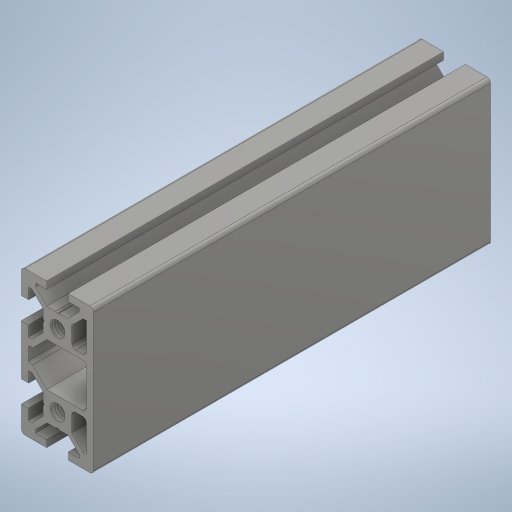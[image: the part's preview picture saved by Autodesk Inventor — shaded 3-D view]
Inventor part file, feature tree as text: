
AUTODESK INVENTOR PART (.ipt)
format: ipt  version: 2024 (Build 280153000, 153)  size: 378,880 bytes
history: native  units: mm
features: other x7, thread x4, sketch x2, extrude x1, hole x1, pattern_linear x1
ambient origin geometry x8: Origin, YZ Plane, XZ Plane, XY Plane, X Axis, Y Axis, Z Axis, Center Point
bodies: Solid1 (feature_tree)
feature tree (16):
  extrude  "Extrusion1"  Depth=20.0mm TaperAngle=0.0deg
  hole  "Hole1"  [1 undecoded]
  pattern_linear  "Rectangular Pattern1"  Spacing1=10.0mm  [1 undecoded]
  other  "C1_XY"
  other  "C1_YZ"
  other  "C1_ZX"
  other  "C1_X"
  other  "C1_Y"
  other  "C1_Z"
  other  "C1_Center"
  thread  "Thread1"  [1 undecoded]
  thread  "Thread2"  [1 undecoded]
  thread  "Thread3"  [1 undecoded]
  thread  "Thread4"  [1 undecoded]
  sketch  "Sketch_63"  dims[d2=4.2mm d3=6.0mm d4=4.0mm d5=2.0mm d6=90.0deg d7=110.0mm d8=0.0mm d9=20.0mm d11=20.0mm d12=10.0mm d14=0.0mm d15=0.0mm d16=10.0mm d17=0.0mm d18=10.0mm d19=0.0mm d20=10.0mm d21=0.0mm d22=10.0mm d23=0.0mm]
  sketch  "Sketch2"  dims[d0=110.0mm d1=0.0mm]
note: 6 required parameter values undecoded (feature->parameter linkage not recoverable at this tier; creation-order binding heuristic only, values carry confidence <= 0.55)
